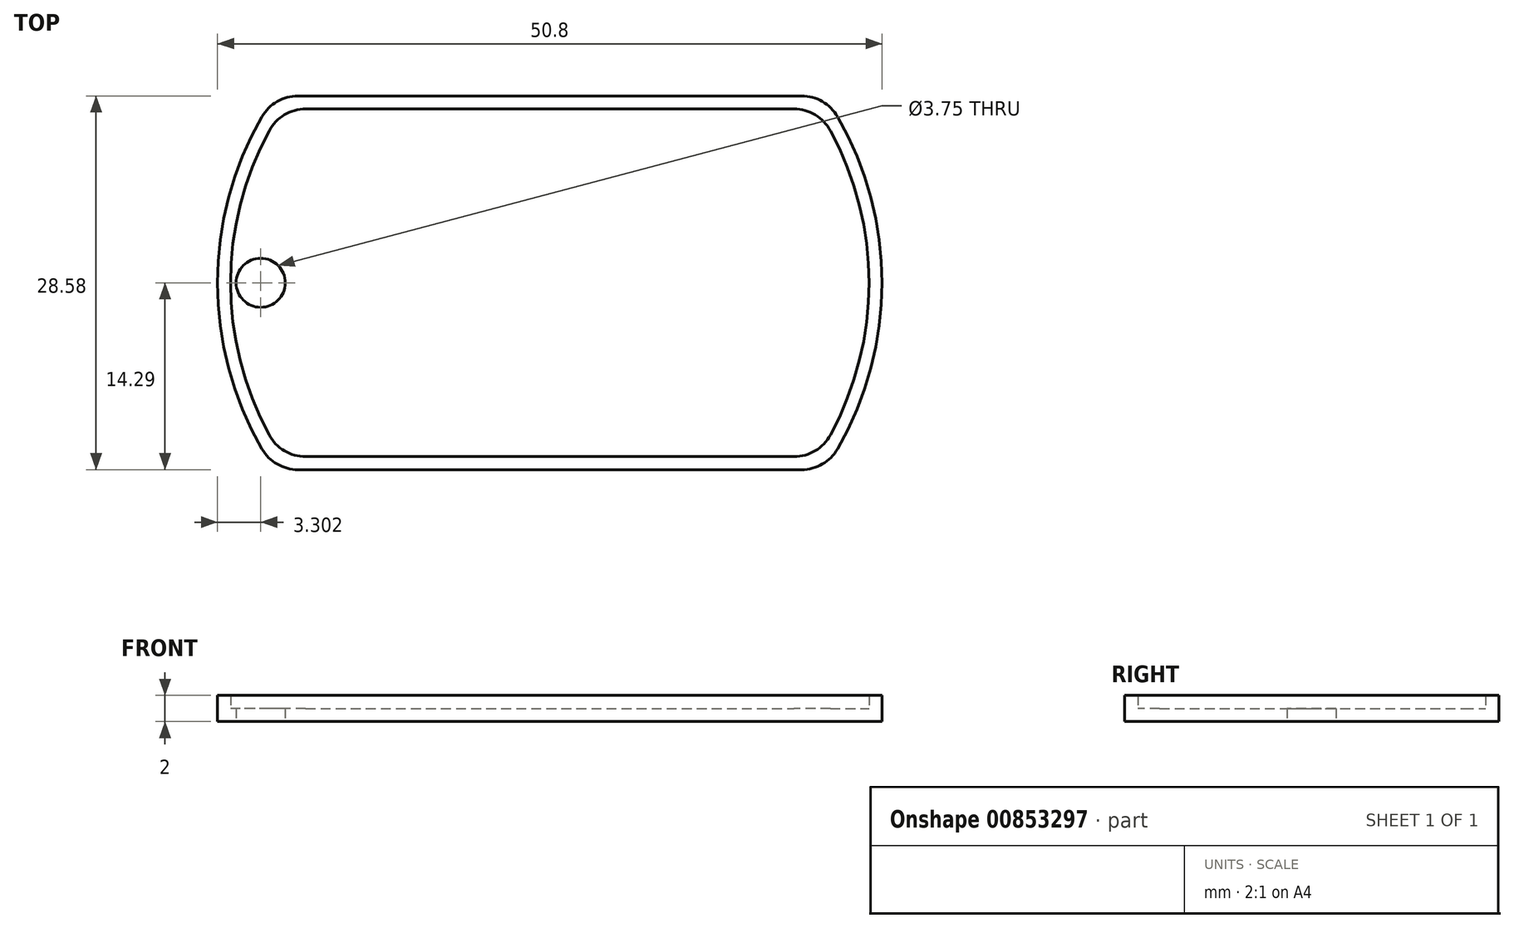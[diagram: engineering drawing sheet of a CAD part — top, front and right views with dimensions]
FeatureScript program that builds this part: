
annotation { "Feature Type Name" : "Feature", "Feature Type Description" : "" }
export const myFeature = defineFeature(function(context is Context, id is Id, definition is map)
    precondition{}
    {
        {
            var Q0;
            Q0=qCreatedBy(makeId("Top.planeOp"),FACE);
            var sketch = newSketch(context, id + "F0", { "sketchPlane" : qUnion([Q0])});
            skArc(sketch, "E0", {"start": v(-22, 12.7) * mm, "mid": v(-25.4, 0) * mm, "end": v(-22, -12.7) * mm});
            skLineSegment(sketch, "E1.top", {"start": v(-19.25, -14.29) * mm, "end": v(19.25, -14.29) * mm});
            skArc(sketch, "E2.trimOffspring", {"start": v(22, -12.7) * mm, "mid": v(25.4, 0) * mm, "end": v(22, 12.7) * mm});
            skLineSegment(sketch, "E3", {"start": v(-19.25, 14.29) * mm, "end": v(19.25, 14.29) * mm});
            skPoint(sketch, "E4.visualSharp", {"position": v(-21, 14.29) * mm});
            skArc(sketch, "E4.filletArc", {"start": v(-19.25, 14.29) * mm, "mid": v(-20.83, 13.86) * mm, "end": v(-22, 12.7) * mm});
            skPoint(sketch, "E5.visualSharp", {"position": v(21, 14.29) * mm});
            skArc(sketch, "E5.filletArc", {"start": v(22, 12.7) * mm, "mid": v(20.83, 13.86) * mm, "end": v(19.25, 14.29) * mm});
            skPoint(sketch, "E6.visualSharp", {"position": v(21, -14.29) * mm});
            skArc(sketch, "E6.filletArc", {"start": v(19.25, -14.29) * mm, "mid": v(20.83, -13.86) * mm, "end": v(22, -12.7) * mm});
            skPoint(sketch, "E7.visualSharp", {"position": v(-21, -14.29) * mm});
            skArc(sketch, "E7.filletArc", {"start": v(-22, -12.7) * mm, "mid": v(-20.83, -13.86) * mm, "end": v(-19.25, -14.29) * mm});
            skCircle(sketch, "E8", {"center": v(-22.1, 0) * mm, "radius": 1.87 * mm});
            skSolve(sketch);
        }
        {
            var Q0;
            Q0=makeQuery(id+"F0.imprint","IMPRINT",FACE,{"disambiguationData":[TD([[makeQuery(id+"F0.imprint","IMPRINT",EDGE,{"derivedFrom":sQuery(id+"F0.wireOp",EDGE,"E0")}),1.0]])]});
            extrude(context, id + "F1", {"entities" : qUnion([Q0]), "depth" : 1 * mm, "offsetDistance" : 25.4 * mm});
        }
        {
            var Q0;
            Q0=makeQuery(id+"F1.opExtrude","CAP_FACE",FACE,{"disambiguationData":[OSD([sQuery(id+"F0.wireOp",EDGE,"E0"),sQuery(id+"F0.wireOp",EDGE,"E1.top"),sQuery(id+"F0.wireOp",EDGE,"E2.trimOffspring"),sQuery(id+"F0.wireOp",EDGE,"E3"),sQuery(id+"F0.wireOp",EDGE,"E4.filletArc"),sQuery(id+"F0.wireOp",EDGE,"E5.filletArc"),sQuery(id+"F0.wireOp",EDGE,"E6.filletArc"),sQuery(id+"F0.wireOp",EDGE,"E7.filletArc")])],"isStart":false});
            var sketch = newSketch(context, id + "F2", { "sketchPlane" : qUnion([Q0])});
            skLineSegment(sketch, "E9.0", {"start": v(-18.66, 13.29) * mm, "end": v(18.66, 13.29) * mm});
            skArc(sketch, "E9.1", {"start": v(-21.45, 11.63) * mm, "mid": v(-24.4, 0) * mm, "end": v(-21.45, -11.63) * mm});
            skLineSegment(sketch, "E9.2", {"start": v(-18.66, -13.29) * mm, "end": v(18.66, -13.29) * mm});
            skArc(sketch, "E9.3", {"start": v(21.45, -11.63) * mm, "mid": v(24.4, 0) * mm, "end": v(21.45, 11.63) * mm});
            skPoint(sketch, "E10.visualSharp", {"position": v(-20.46, 13.29) * mm});
            skArc(sketch, "E10.filletArc", {"start": v(-18.66, 13.29) * mm, "mid": v(-20.29, 12.84) * mm, "end": v(-21.45, 11.63) * mm});
            skPoint(sketch, "E11.visualSharp", {"position": v(20.46, 13.29) * mm});
            skArc(sketch, "E11.filletArc", {"start": v(21.45, 11.63) * mm, "mid": v(20.29, 12.84) * mm, "end": v(18.66, 13.29) * mm});
            skPoint(sketch, "E12.visualSharp", {"position": v(20.46, -13.29) * mm});
            skArc(sketch, "E12.filletArc", {"start": v(18.66, -13.29) * mm, "mid": v(20.29, -12.84) * mm, "end": v(21.45, -11.63) * mm});
            skPoint(sketch, "E13.visualSharp", {"position": v(-20.46, -13.29) * mm});
            skArc(sketch, "E13.filletArc", {"start": v(-21.45, -11.63) * mm, "mid": v(-20.29, -12.84) * mm, "end": v(-18.66, -13.29) * mm});
            skLineSegment(sketch, "E14.0", {"start": v(-19.25, 14.29) * mm, "end": v(19.25, 14.29) * mm});
            skArc(sketch, "E14.1", {"start": v(-22, 12.7) * mm, "mid": v(-25.4, 0) * mm, "end": v(-22, -12.7) * mm});
            skLineSegment(sketch, "E14.2", {"start": v(-19.25, -14.29) * mm, "end": v(19.25, -14.29) * mm});
            skArc(sketch, "E14.3", {"start": v(22, -12.7) * mm, "mid": v(25.4, 0) * mm, "end": v(22, 12.7) * mm});
            skPoint(sketch, "E15.visualSharp", {"position": v(-21, -14.29) * mm});
            skArc(sketch, "E15.filletArc", {"start": v(-22, -12.7) * mm, "mid": v(-20.83, -13.86) * mm, "end": v(-19.25, -14.29) * mm});
            skPoint(sketch, "E16.visualSharp", {"position": v(21, -14.29) * mm});
            skArc(sketch, "E16.filletArc", {"start": v(19.25, -14.29) * mm, "mid": v(20.83, -13.86) * mm, "end": v(22, -12.7) * mm});
            skPoint(sketch, "E17.visualSharp", {"position": v(21, 14.29) * mm});
            skArc(sketch, "E17.filletArc", {"start": v(22, 12.7) * mm, "mid": v(20.83, 13.86) * mm, "end": v(19.25, 14.29) * mm});
            skPoint(sketch, "E18.visualSharp", {"position": v(-21, 14.29) * mm});
            skArc(sketch, "E18.filletArc", {"start": v(-19.25, 14.29) * mm, "mid": v(-20.83, 13.86) * mm, "end": v(-22, 12.7) * mm});
            skSolve(sketch);
        }
        {
            var Q0;
            Q0=makeQuery(id+"F2.imprint","IMPRINT",FACE,{"disambiguationData":[TD([[makeQuery(id+"F2.imprint","IMPRINT",EDGE,{"derivedFrom":sQuery(id+"F2.wireOp",EDGE,"E9.0")}),1.0]])]});
            extrude(context, id + "F3", {"entities" : qUnion([Q0]), "operationType" : NewBodyOperationType.ADD, "depth" : 1 * mm, "offsetDistance" : 25.4 * mm});
        }
        {
            var Q0;
            Q0=makeQuery(id+"F1.opExtrude","CAP_FACE",FACE,{"disambiguationData":[OSD([sQuery(id+"F0.wireOp",EDGE,"E0"),sQuery(id+"F0.wireOp",EDGE,"E1.top"),sQuery(id+"F0.wireOp",EDGE,"E2.trimOffspring"),sQuery(id+"F0.wireOp",EDGE,"E3"),sQuery(id+"F0.wireOp",EDGE,"E4.filletArc"),sQuery(id+"F0.wireOp",EDGE,"E5.filletArc"),sQuery(id+"F0.wireOp",EDGE,"E6.filletArc"),sQuery(id+"F0.wireOp",EDGE,"E7.filletArc"),sQuery(id+"F0.wireOp",EDGE,"E8")])],"isStart":false});
            var sketch = newSketch(context, id + "F4", { "sketchPlane" : qUnion([Q0])});
            skText(sketch, "E19", { "text": "BRINK", "fontName": "OpenSans-Bold.ttf"});
            const initialGuessF4  = {"E19": [-0.02006, -0.00503, 1, 0, 0.00987]};
            skSetInitialGuess(sketch, initialGuessF4);
            skSolve(sketch);
        }
        {
            var Q0;
            Q0 = qConstructionFilter(qBodyType(qCreatedBy(id + "F4" ,EDGE), BodyType.WIRE), ConstructionObject.NO);
            extrude(context, id + "F5", {"bodyType" : ToolBodyType.SURFACE, "surfaceEntities" : qUnion([Q0]), "depth" : 5.08 * mm, "offsetDistance" : 25.4 * mm});
        }
    });
